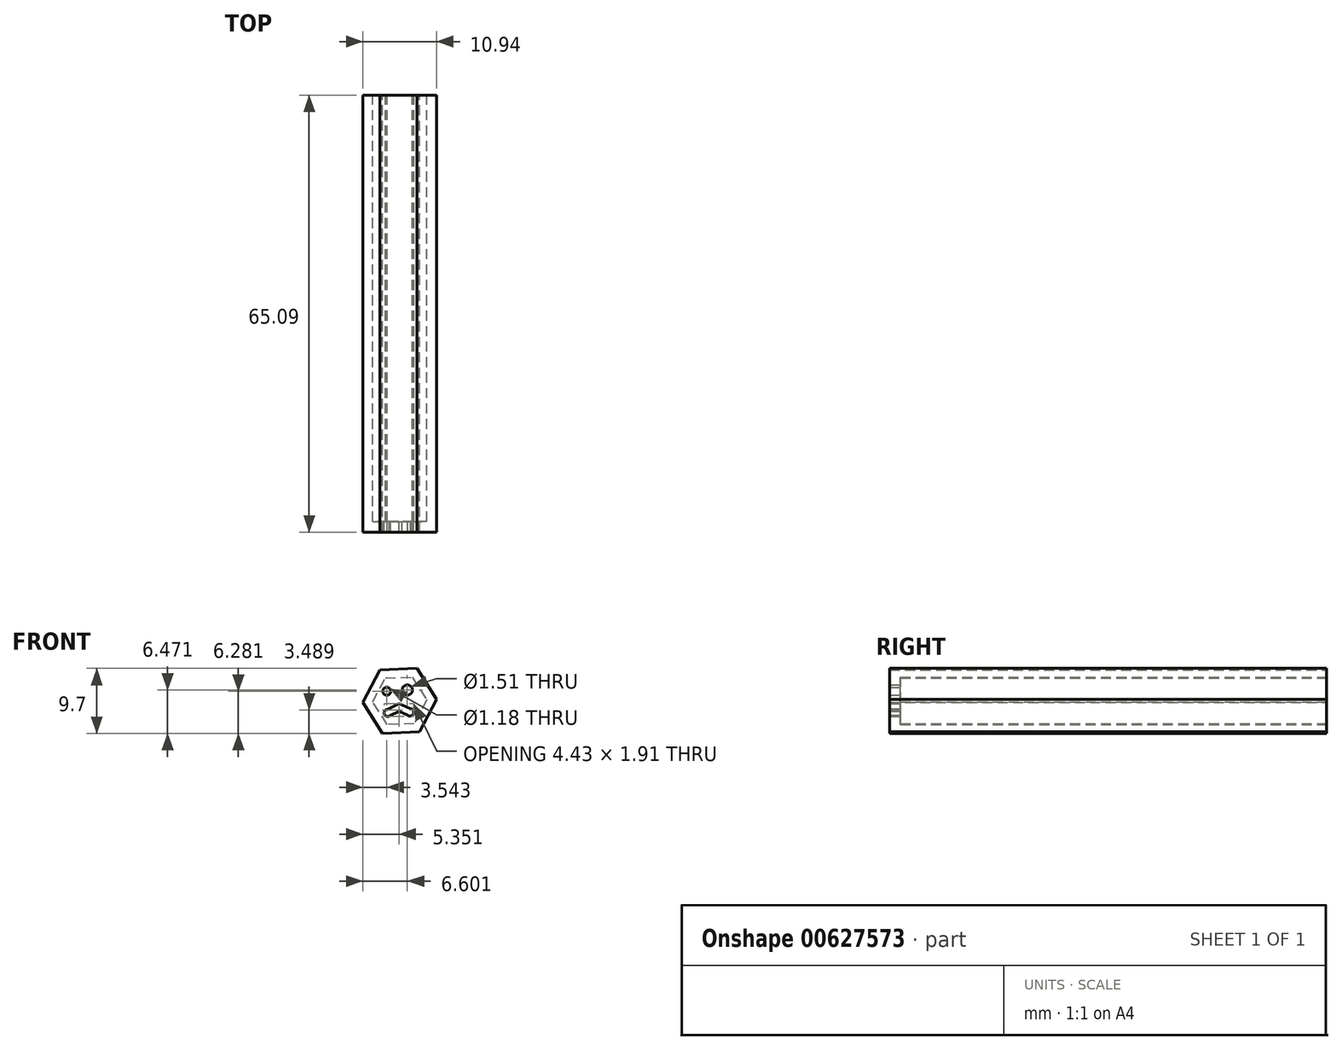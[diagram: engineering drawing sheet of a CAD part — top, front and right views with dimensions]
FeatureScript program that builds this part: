
annotation { "Feature Type Name" : "Feature", "Feature Type Description" : "" }
export const myFeature = defineFeature(function(context is Context, id is Id, definition is map)
    precondition{}
    {
        {
            var Q0;
            Q0=qCreatedBy(makeId("Front.planeOp"),FACE);
            var sketch = newSketch(context, id + "F0", { "sketchPlane" : qUnion([Q0])});
            skCircle(sketch, "E0.cCircle", {"center": v(0, 0) * mm, "radius": 3.47 * mm, "construction": true});
            skLineSegment(sketch, "E0.0", {"start": v(1.86, 3.55) * mm, "end": v(4, 0.16) * mm});
            skLineSegment(sketch, "E0.1", {"start": v(4, 0.16) * mm, "end": v(2.15, -3.39) * mm});
            skLineSegment(sketch, "E0.2", {"start": v(2.15, -3.39) * mm, "end": v(-1.86, -3.55) * mm});
            skLineSegment(sketch, "E0.3", {"start": v(-1.86, -3.55) * mm, "end": v(-4, -0.16) * mm});
            skLineSegment(sketch, "E0.4", {"start": v(-4, -0.16) * mm, "end": v(-2.15, 3.39) * mm});
            skLineSegment(sketch, "E0.5", {"start": v(-2.15, 3.39) * mm, "end": v(1.86, 3.55) * mm});
            skPoint(sketch, "E0.0.midPoint", {"position": v(2.93, 1.86) * mm});
            skCircle(sketch, "E1.cCircle", {"center": v(0, 0) * mm, "radius": 4.74 * mm, "construction": true});
            skLineSegment(sketch, "E1.0", {"start": v(2.54, 4.85) * mm, "end": v(5.47, 0.22) * mm});
            skLineSegment(sketch, "E1.1", {"start": v(5.47, 0.22) * mm, "end": v(2.93, -4.63) * mm});
            skLineSegment(sketch, "E1.2", {"start": v(2.93, -4.63) * mm, "end": v(-2.54, -4.85) * mm});
            skLineSegment(sketch, "E1.3", {"start": v(-2.54, -4.85) * mm, "end": v(-5.47, -0.22) * mm});
            skLineSegment(sketch, "E1.4", {"start": v(-5.47, -0.22) * mm, "end": v(-2.93, 4.63) * mm});
            skLineSegment(sketch, "E1.5", {"start": v(-2.93, 4.63) * mm, "end": v(2.54, 4.85) * mm});
            skPoint(sketch, "E1.0.midPoint", {"position": v(4, 2.54) * mm});
            skSolve(sketch);
        }
        {
            var Q0;
            Q0=makeQuery(id+"F0.imprint","IMPRINT",FACE,{"disambiguationData":[TD([[makeQuery(id+"F0.imprint","IMPRINT",EDGE,{"derivedFrom":sQuery(id+"F0.wireOp",EDGE,"E0.0")}),1.0]])]});
            extrude(context, id + "F1", {"entities" : qUnion([Q0]), "endBound" : BoundingType.SYMMETRIC, "depth" : 63.5 * mm, "offsetDistance" : 25.4 * mm});
        }
        {
            var Q0;
            Q0=makeQuery(id+"F1.opExtrude","CAP_FACE",FACE,{"disambiguationData":[OSD([sQuery(id+"F0.wireOp",EDGE,"E0.0"),sQuery(id+"F0.wireOp",EDGE,"E0.1"),sQuery(id+"F0.wireOp",EDGE,"E0.2"),sQuery(id+"F0.wireOp",EDGE,"E0.3"),sQuery(id+"F0.wireOp",EDGE,"E0.4"),sQuery(id+"F0.wireOp",EDGE,"E0.5"),sQuery(id+"F0.wireOp",EDGE,"E1.0"),sQuery(id+"F0.wireOp",EDGE,"E1.1"),sQuery(id+"F0.wireOp",EDGE,"E1.2"),sQuery(id+"F0.wireOp",EDGE,"E1.3"),sQuery(id+"F0.wireOp",EDGE,"E1.4"),sQuery(id+"F0.wireOp",EDGE,"E1.5")])],"isStart":false});
            var sketch = newSketch(context, id + "F2", { "sketchPlane" : qUnion([Q0])});
            skLineSegment(sketch, "E2", {"start": v(-4, -0.16) * mm, "end": v(-2.15, 3.39) * mm});
            skLineSegment(sketch, "E3", {"start": v(-2.15, 3.39) * mm, "end": v(1.86, 3.55) * mm});
            skLineSegment(sketch, "E4", {"start": v(1.86, 3.55) * mm, "end": v(4, 0.16) * mm});
            skLineSegment(sketch, "E5", {"start": v(4, 0.16) * mm, "end": v(2.15, -3.39) * mm});
            skLineSegment(sketch, "E6", {"start": v(2.15, -3.39) * mm, "end": v(-1.86, -3.55) * mm});
            skLineSegment(sketch, "E7", {"start": v(-1.86, -3.55) * mm, "end": v(-4, -0.16) * mm});
            skCircle(sketch, "E8", {"center": v(-1.93, 1.43) * mm, "radius": 0.59 * mm});
            skCircle(sketch, "E9", {"center": v(1.13, 1.62) * mm, "radius": 0.76 * mm});
            skArc(sketch, "E10", {"start": v(-1.9, -1.28) * mm, "mid": v(-2.3, -1.97) * mm, "end": v(-1.56, -2.25) * mm});
            skArc(sketch, "E11", {"start": v(1.18, -2.14) * mm, "mid": v(2.04, -1.95) * mm, "end": v(1.63, -1.16) * mm});
            skLineSegment(sketch, "E12", {"start": v(-1.9, -1.28) * mm, "end": v(-0.08, -0.4) * mm});
            skLineSegment(sketch, "E13", {"start": v(-0.08, -0.4) * mm, "end": v(1.88, -1.27) * mm});
            skLineSegment(sketch, "E14", {"start": v(-1.6, -2.28) * mm, "end": v(-0.11, -1.56) * mm});
            skLineSegment(sketch, "E15", {"start": v(-0.11, -1.56) * mm, "end": v(1.18, -2.14) * mm});
            skSolve(sketch);
        }
        {
            var Q0;
            Q0=makeQuery(id+"F2.imprint","IMPRINT",FACE,{"disambiguationData":[TD([[makeQuery(id+"F2.imprint","IMPRINT",EDGE,{"derivedFrom":sQuery(id+"F2.wireOp",EDGE,"E2")}),-1.0]])]});
            var Q1;
            Q1=makeQuery(id+"F2.imprint","IMPRINT",FACE,{"disambiguationData":[TD([[makeQuery(id+"F2.imprint","IMPRINT",EDGE,{"derivedFrom":sQuery(id+"F2.wireOp",EDGE,"E2")}),1.0]])]});
            extrude(context, id + "F3", {"entities" : qUnion([Q0, Q1]), "operationType" : NewBodyOperationType.ADD, "depth" : 1.59 * mm, "offsetDistance" : 25.4 * mm});
        }
    });
